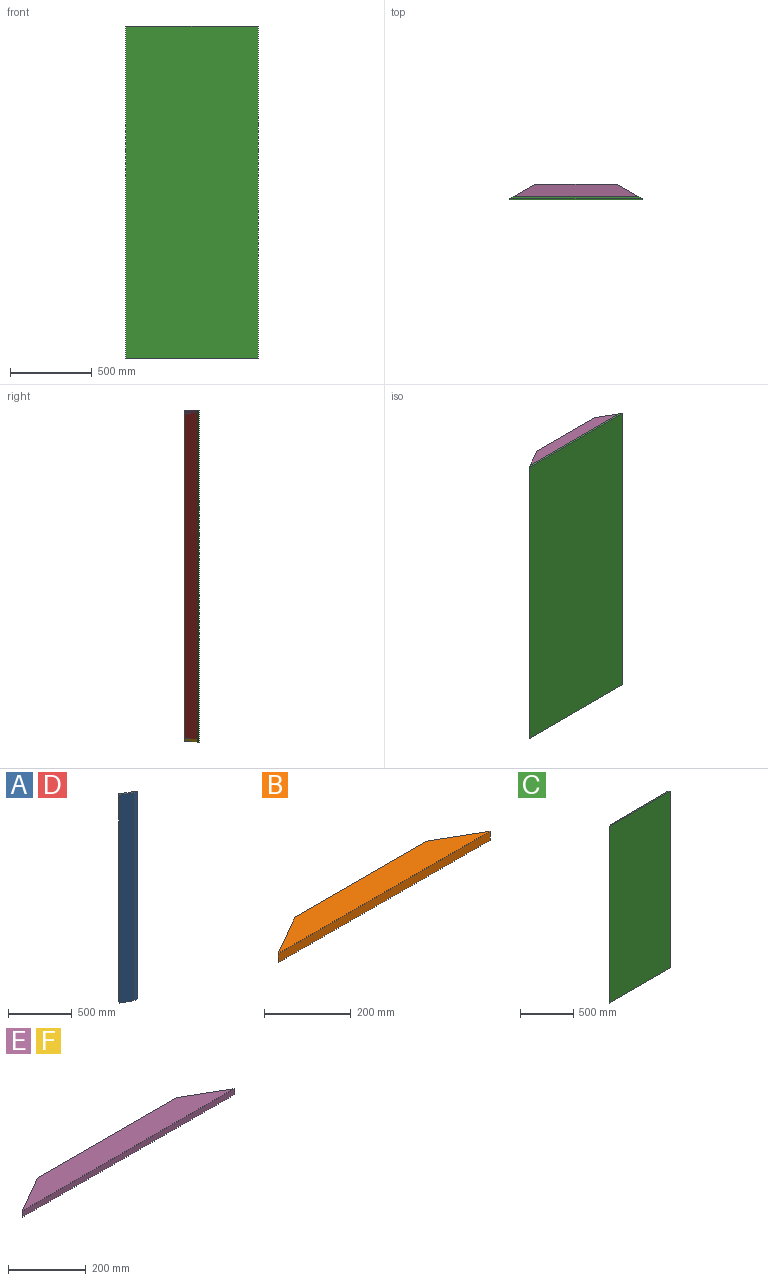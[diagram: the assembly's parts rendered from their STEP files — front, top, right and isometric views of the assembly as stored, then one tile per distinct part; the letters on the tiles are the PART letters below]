
ASSEMBLY  parts=6 mates=5
PART A: 6 faces, bbox 141.5x76.2x1993.9 mm
  f0: plane 141.51x76.2mm, normal (0,0,1), area 2588.9mm2, adj f1,f2,f3,f4
  f1: plane 1993.9x38.1mm, normal (0,-1,0), area 75967.6mm2, adj f0,f2,f4,f5
  f2: plane 1993.9x131.98mm, normal (0.5,0.87,0), area 303870.4mm2, adj f0,f1,f3,f5
  f3: plane 1993.9x16.5mm, normal (-0.87,0.5,0), area 37983.8mm2, adj f0,f2,f4,f5
  f4: plane 1993.9x103.41mm, normal (-0.5,-0.87,0), area 238080.5mm2, adj f0,f1,f3,f5
  f5: plane 141.51x76.2mm, normal (0,0,-1), area 2588.9mm2, adj f1,f2,f3,f4
PART B: 6 faces, bbox 692.6x76.2x25.4 mm
  f0: plane 428.64x25.4mm, normal (0,1,0), area 10887.5mm2, adj f1,f3,f4,f5
  f1: plane 131.98x76.2mm, normal (-0.5,0.87,0), area 3871mm2, adj f0,f2,f4,f5
  f2: plane 692.61x25.4mm, normal (0,-1,0), area 17592.2mm2, adj f1,f3,f4,f5
  f3: plane 131.98x76.2mm, normal (0.5,0.87,0), area 3871mm2, adj f0,f2,f4,f5
  f4: plane 692.61x76.2mm, normal (0,0,1), area 42719.5mm2, adj f0,f1,f2,f3
  f5: plane 692.61x76.2mm, normal (0,0,-1), area 42719.5mm2, adj f0,f1,f2,f3
PART C: 6 faces, bbox 812.8x12.7x2032 mm
  f0: plane 2032x22mm, normal (-0.5,0.87,0), area 51612.8mm2, adj f1,f3,f4,f5
  f1: plane 2032x812.8mm, normal (0,-1,0), area 1651609.6mm2, adj f0,f2,f4,f5
  f2: plane 2032x22mm, normal (0.5,0.87,0), area 51612.8mm2, adj f1,f3,f4,f5
  f3: plane 2032x768.81mm, normal (0,1,0), area 1562213.6mm2, adj f0,f2,f4,f5
  f4: plane 812.8x12.7mm, normal (0,0,1), area 10043.2mm2, adj f0,f1,f2,f3
  f5: plane 812.8x12.7mm, normal (0,0,-1), area 10043.2mm2, adj f0,f1,f2,f3
PART D: same geometry as A
PART E: 6 faces, bbox 768.8x76.2x19.1 mm
  f0: plane 131.98x76.2mm, normal (-0.5,0.87,0), area 2903.2mm2, adj f1,f3,f4,f5
  f1: plane 768.81x19.05mm, normal (0,-1,0), area 14645.8mm2, adj f0,f2,f4,f5
  f2: plane 131.98x76.2mm, normal (0.5,0.87,0), area 2903.2mm2, adj f1,f3,f4,f5
  f3: plane 504.84x19.05mm, normal (0,1,0), area 9617.2mm2, adj f0,f2,f4,f5
  f4: plane 768.81x76.2mm, normal (0,0,-1), area 48526mm2, adj f0,f1,f2,f3
  f5: plane 768.81x76.2mm, normal (0,0,1), area 48526mm2, adj f0,f1,f2,f3
PART F: same geometry as E
PLACE A t=(69.71,7.77,-24.94)mm
PLACE B t=(69.71,7.77,-24.94)mm
PLACE C t=(69.71,7.77,-24.94)mm
PLACE D rot(axis=(0,-1,0),180deg) t=(69.71,7.77,-24.94)mm
PLACE E t=(69.71,7.77,-24.94)mm
PLACE F rot(axis=(0,1,0),180deg) t=(69.71,7.77,-24.94)mm
MATE fastened A.f2 <-> E.f2  axis (0.5,0.87,0) through (454.11,-214.17,972.01)mm
MATE fastened F.f2 <-> D.f2  axis (-0.5,0.87,0) through (-314.7,-214.17,-1021.89)mm
MATE fastened C.f3 <-> B.f2  axis (0,1,0) through (69.71,-214.17,-24.94)mm
MATE fastened E.f2 <-> C.f2  axis (0.5,0.87,0) through (454.11,-214.17,991.06)mm
MATE fastened D.f2 <-> E.f0  axis (-0.5,0.87,0) through (-314.7,-214.17,972.01)mm
